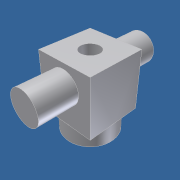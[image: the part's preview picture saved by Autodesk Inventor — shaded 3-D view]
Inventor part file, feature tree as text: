
AUTODESK INVENTOR PART (.ipt)
format: ipt  version: unknown  size: 187,392 bytes
history: native  units: mm
features: extrude x4, sketch x4
ambient origin geometry x8: Origin, YZ Plane, XZ Plane, XY Plane, X Axis, Y Axis, Z Axis, Center Point
feature tree (8):
  extrude  "Выдавливание1"  Depth=1.2mm
  extrude  "Выдавливание2"  Depth=3.4mm
  extrude  "Выдавливание3"  Depth=1.15mm TaperAngle=0.0deg
  extrude  "Выдавливание4"  Depth=3.5mm TaperAngle=0.0deg
  sketch  "Эскиз1"
  sketch  "Эскиз2"
  sketch  "Эскиз3"
  sketch  "Эскиз4"
